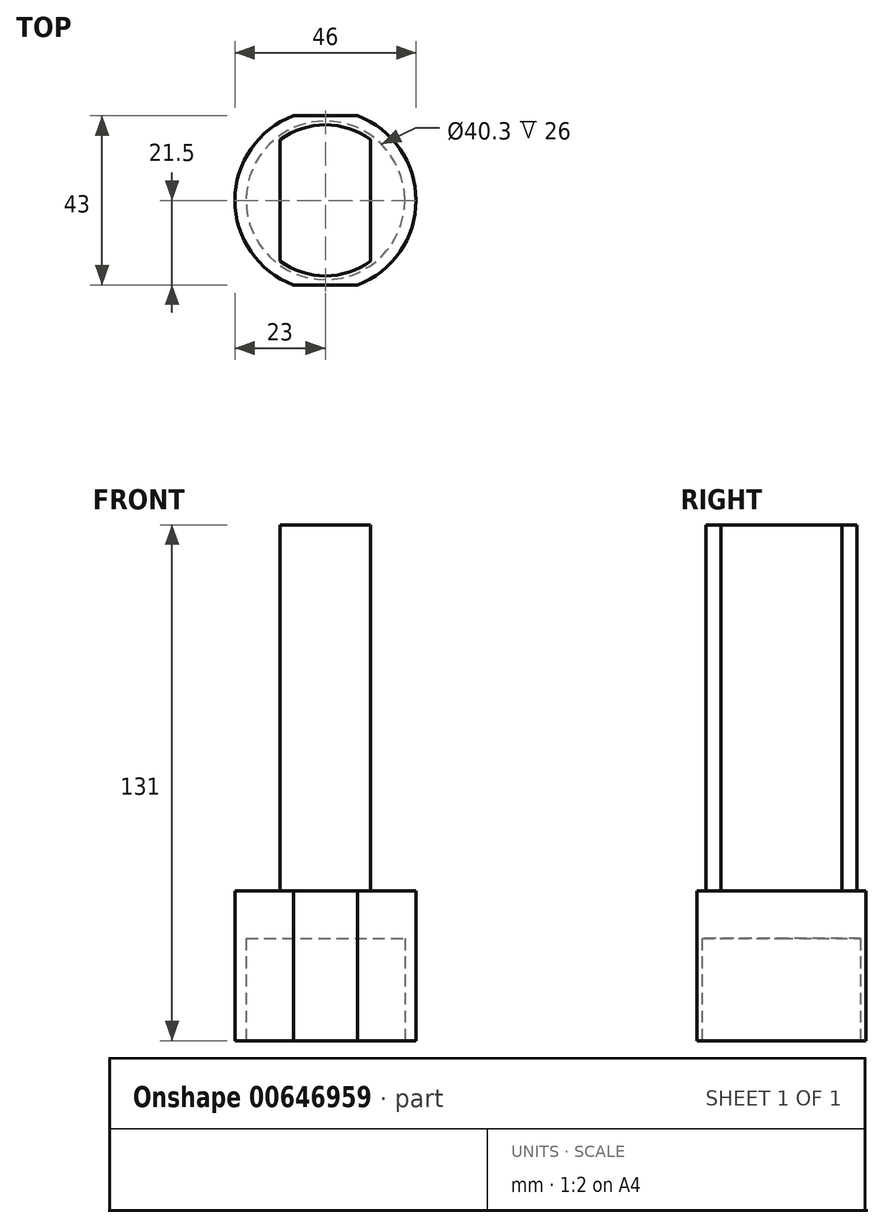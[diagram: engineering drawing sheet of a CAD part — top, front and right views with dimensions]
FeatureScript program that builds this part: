
annotation { "Feature Type Name" : "Feature", "Feature Type Description" : "" }
export const myFeature = defineFeature(function(context is Context, id is Id, definition is map)
    precondition{}
    {
        {
            var Q0;
            Q0=qCreatedBy(makeId("Top.planeOp"),FACE);
            var sketch = newSketch(context, id + "F0", { "sketchPlane" : qUnion([Q0])});
            skArc(sketch, "E0", {"start": v(8.17, -21.5) * mm, "mid": v(23, 0) * mm, "end": v(8.17, 21.5) * mm});
            skLineSegment(sketch, "E1", {"start": v(-8.17, -21.5) * mm, "end": v(8.17, -21.5) * mm});
            skLineSegment(sketch, "E2.MirrorCS", {"start": v(-8.17, 21.5) * mm, "end": v(8.17, 21.5) * mm});
            skArc(sketch, "E3.trimOffspring", {"start": v(-8.17, 21.5) * mm, "mid": v(-23, 0) * mm, "end": v(-8.17, -21.5) * mm});
            skSolve(sketch);
        }
        {
            var Q0;
            Q0=makeQuery(id+"F0.imprint","IMPRINT",FACE,{"disambiguationData":[TD([[makeQuery(id+"F0.imprint","IMPRINT",EDGE,{"derivedFrom":sQuery(id+"F0.wireOp",EDGE,"E0")}),1.0]])]});
            extrude(context, id + "F1", {"entities" : qUnion([Q0]), "depth" : 38 * mm, "offsetDistance" : 25 * mm});
        }
        {
            var Q0;
            Q0=makeQuery(id+"F1.opExtrude","CAP_FACE",FACE,{"disambiguationData":[OSD([sQuery(id+"F0.wireOp",EDGE,"E0"),sQuery(id+"F0.wireOp",EDGE,"E1"),sQuery(id+"F0.wireOp",EDGE,"E2.MirrorCS"),sQuery(id+"F0.wireOp",EDGE,"E3.trimOffspring")])],"isStart":true});
            var sketch = newSketch(context, id + "F2", { "sketchPlane" : qUnion([Q0])});
            skCircle(sketch, "E4", {"center": v(0, 0) * mm, "radius": 20.15 * mm});
            skSolve(sketch);
        }
        {
            var Q0;
            Q0=makeQuery(id+"F2.imprint","IMPRINT",FACE,{"disambiguationData":[TD([[makeQuery(id+"F2.imprint","IMPRINT",EDGE,{"derivedFrom":sQuery(id+"F2.wireOp",EDGE,"E4")}),1.0]])]});
            extrude(context, id + "F3", {"entities" : qUnion([Q0]), "operationType" : NewBodyOperationType.REMOVE, "oppositeDirection" : true, "depth" : 26 * mm, "offsetDistance" : 25 * mm});
        }
        {
            var Q0;
            Q0=makeQuery(id+"F1.opExtrude","CAP_FACE",FACE,{"disambiguationData":[OSD([sQuery(id+"F0.wireOp",EDGE,"E0"),sQuery(id+"F0.wireOp",EDGE,"E1"),sQuery(id+"F0.wireOp",EDGE,"E2.MirrorCS"),sQuery(id+"F0.wireOp",EDGE,"E3.trimOffspring")])],"isStart":false});
            var sketch = newSketch(context, id + "F4", { "sketchPlane" : qUnion([Q0])});
            skArc(sketch, "E5", {"start": v(11.5, 15.37) * mm, "mid": v(0, 19.2) * mm, "end": v(-11.5, 15.37) * mm});
            skLineSegment(sketch, "E6", {"start": v(11.5, -15.37) * mm, "end": v(11.5, 15.37) * mm});
            skLineSegment(sketch, "E7.MirrorCS", {"start": v(-11.5, -15.37) * mm, "end": v(-11.5, 15.37) * mm});
            skArc(sketch, "E8.trimOffspring", {"start": v(-11.5, -15.37) * mm, "mid": v(0, -19.2) * mm, "end": v(11.5, -15.37) * mm});
            skSolve(sketch);
        }
        {
            var Q0;
            Q0 = qSketchRegion(id + "F4", true);
            extrude(context, id + "F5", {"entities" : qUnion([Q0]), "operationType" : NewBodyOperationType.ADD, "depth" : 93 * mm, "offsetDistance" : 25 * mm});
        }
    });
